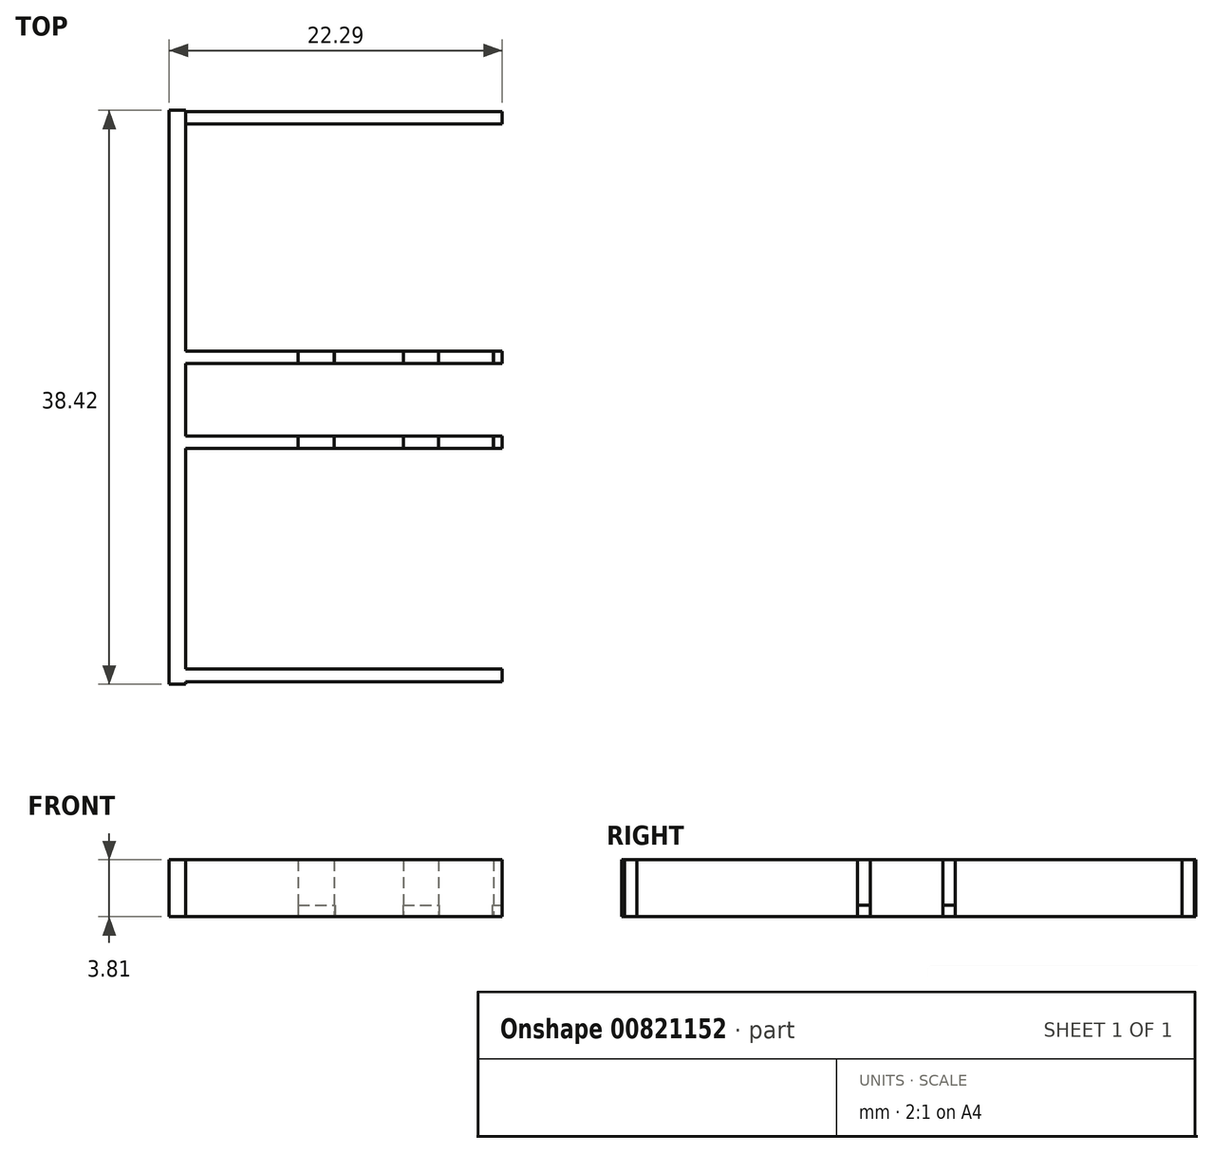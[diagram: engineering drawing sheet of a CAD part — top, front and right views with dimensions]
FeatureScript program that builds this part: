
annotation { "Feature Type Name" : "Feature", "Feature Type Description" : "" }
export const myFeature = defineFeature(function(context is Context, id is Id, definition is map)
    precondition{}
    {
        {
            var Q0;
            Q0=qCreatedBy(makeId("Top.planeOp"),FACE);
            var sketch = newSketch(context, id + "F0", { "sketchPlane" : qUnion([Q0])});
            skLineSegment(sketch, "E0.bottom", {"start": v(-54.97, 0.72) * mm, "end": v(-76.14, 0.72) * mm});
            skLineSegment(sketch, "E0.top", {"start": v(-54.97, -0.12) * mm, "end": v(-76.14, -0.12) * mm});
            skLineSegment(sketch, "E0.left", {"start": v(-54.97, 0.72) * mm, "end": v(-54.97, -0.12) * mm});
            skLineSegment(sketch, "E0.right", {"start": v(-76.14, 0.72) * mm, "end": v(-76.14, -0.12) * mm});
            skLineSegment(sketch, "E1.bottom", {"start": v(-66.2, -15.3) * mm, "end": v(-61.58, -15.3) * mm});
            skLineSegment(sketch, "E1.top", {"start": v(-66.2, -16.14) * mm, "end": v(-61.58, -16.14) * mm});
            skLineSegment(sketch, "E1.left", {"start": v(-66.2, -15.3) * mm, "end": v(-66.2, -16.14) * mm});
            skLineSegment(sketch, "E1.right", {"start": v(-61.58, -15.3) * mm, "end": v(-61.58, -16.14) * mm});
            skLineSegment(sketch, "E2.bottom", {"start": v(-66.2, -20.99) * mm, "end": v(-61.58, -20.99) * mm});
            skLineSegment(sketch, "E2.top", {"start": v(-66.2, -21.83) * mm, "end": v(-61.58, -21.83) * mm});
            skLineSegment(sketch, "E2.left", {"start": v(-66.2, -20.99) * mm, "end": v(-66.2, -21.83) * mm});
            skLineSegment(sketch, "E2.right", {"start": v(-61.58, -20.99) * mm, "end": v(-61.58, -21.83) * mm});
            skLineSegment(sketch, "E3.bottom", {"start": v(-59.25, -21.83) * mm, "end": v(-55.56, -21.83) * mm});
            skLineSegment(sketch, "E3.top", {"start": v(-59.25, -20.99) * mm, "end": v(-55.56, -20.99) * mm});
            skLineSegment(sketch, "E3.left", {"start": v(-59.25, -21.83) * mm, "end": v(-59.25, -20.99) * mm});
            skLineSegment(sketch, "E3.right", {"start": v(-55.56, -21.83) * mm, "end": v(-55.56, -20.99) * mm});
            skLineSegment(sketch, "E4.bottom", {"start": v(-59.25, -15.3) * mm, "end": v(-55.56, -15.3) * mm});
            skLineSegment(sketch, "E4.top", {"start": v(-59.25, -16.14) * mm, "end": v(-55.56, -16.14) * mm});
            skLineSegment(sketch, "E4.left", {"start": v(-59.25, -15.3) * mm, "end": v(-59.25, -16.14) * mm});
            skLineSegment(sketch, "E4.right", {"start": v(-55.56, -15.3) * mm, "end": v(-55.56, -16.14) * mm});
            skLineSegment(sketch, "E5.bottom", {"start": v(-77.25, -15.3) * mm, "end": v(-68.62, -15.3) * mm});
            skLineSegment(sketch, "E5.top", {"start": v(-77.25, -16.14) * mm, "end": v(-68.62, -16.14) * mm});
            skLineSegment(sketch, "E5.left", {"start": v(-77.25, -15.3) * mm, "end": v(-77.25, -16.14) * mm});
            skLineSegment(sketch, "E5.right", {"start": v(-68.62, -15.3) * mm, "end": v(-68.62, -16.14) * mm});
            skLineSegment(sketch, "E6.bottom", {"start": v(-77.25, -20.99) * mm, "end": v(-68.62, -20.99) * mm});
            skLineSegment(sketch, "E6.top", {"start": v(-77.25, -21.83) * mm, "end": v(-68.62, -21.83) * mm});
            skLineSegment(sketch, "E6.left", {"start": v(-77.25, -20.99) * mm, "end": v(-77.25, -21.83) * mm});
            skLineSegment(sketch, "E6.right", {"start": v(-68.62, -20.99) * mm, "end": v(-68.62, -21.83) * mm});
            skLineSegment(sketch, "E7.bottom", {"start": v(-77.2, -36.6) * mm, "end": v(-54.97, -36.6) * mm});
            skLineSegment(sketch, "E7.top", {"start": v(-77.2, -37.43) * mm, "end": v(-54.97, -37.43) * mm});
            skLineSegment(sketch, "E7.left", {"start": v(-77.2, -36.6) * mm, "end": v(-77.2, -37.43) * mm});
            skLineSegment(sketch, "E7.right", {"start": v(-54.97, -36.6) * mm, "end": v(-54.97, -37.43) * mm});
            skLineSegment(sketch, "E8.left", {"start": v(-77.26, 0.8) * mm, "end": v(-77.26, -37.6) * mm});
            skLineSegment(sketch, "E8.right", {"start": v(-76.15, 0.8) * mm, "end": v(-76.15, -37.6) * mm});
            skLineSegment(sketch, "E9", {"start": v(-54.97, -37.6) * mm, "end": v(-54.97, 0.8) * mm});
            skLineSegment(sketch, "E10", {"start": v(-77.26, -37.6) * mm, "end": v(-76.15, -37.6) * mm});
            skLineSegment(sketch, "E11", {"start": v(-77.26, 0.8) * mm, "end": v(-76.15, 0.8) * mm});
            skSolve(sketch);
        }
        {
            var Q0;
            Q0 = qSketchRegion(id + "F0", true);
            extrude(context, id + "F1", {"entities" : qUnion([Q0]), "depth" : 3.8 * mm, "offsetDistance" : 25.4 * mm});
        }
        {
            var Q0;
            Q0=qCreatedBy(makeId("Top.planeOp"),FACE);
            var sketch = newSketch(context, id + "F2", { "sketchPlane" : qUnion([Q0])});
            skLineSegment(sketch, "E12.bottom", {"start": v(-68.62, -15.3) * mm, "end": v(-66.16, -15.3) * mm});
            skLineSegment(sketch, "E12.top", {"start": v(-68.62, -16.14) * mm, "end": v(-66.16, -16.14) * mm});
            skLineSegment(sketch, "E12.left", {"start": v(-68.62, -15.3) * mm, "end": v(-68.62, -16.14) * mm});
            skLineSegment(sketch, "E12.right", {"start": v(-66.16, -15.3) * mm, "end": v(-66.16, -16.14) * mm});
            skLineSegment(sketch, "E13.bottom", {"start": v(-68.64, -20.99) * mm, "end": v(-66.18, -20.99) * mm});
            skLineSegment(sketch, "E13.top", {"start": v(-68.64, -21.83) * mm, "end": v(-66.18, -21.83) * mm});
            skLineSegment(sketch, "E13.left", {"start": v(-68.64, -20.99) * mm, "end": v(-68.64, -21.83) * mm});
            skLineSegment(sketch, "E13.right", {"start": v(-66.18, -20.99) * mm, "end": v(-66.18, -21.83) * mm});
            skLineSegment(sketch, "E14.bottom", {"start": v(-61.62, -15.3) * mm, "end": v(-59.2, -15.3) * mm});
            skLineSegment(sketch, "E14.top", {"start": v(-61.62, -16.14) * mm, "end": v(-59.2, -16.14) * mm});
            skLineSegment(sketch, "E14.left", {"start": v(-61.62, -15.3) * mm, "end": v(-61.62, -16.14) * mm});
            skLineSegment(sketch, "E14.right", {"start": v(-59.2, -15.3) * mm, "end": v(-59.2, -16.14) * mm});
            skLineSegment(sketch, "E15.bottom", {"start": v(-61.6, -20.99) * mm, "end": v(-59.19, -20.99) * mm});
            skLineSegment(sketch, "E15.top", {"start": v(-61.6, -21.83) * mm, "end": v(-59.19, -21.83) * mm});
            skLineSegment(sketch, "E15.left", {"start": v(-61.6, -20.99) * mm, "end": v(-61.6, -21.83) * mm});
            skLineSegment(sketch, "E15.right", {"start": v(-59.19, -20.99) * mm, "end": v(-59.19, -21.83) * mm});
            skLineSegment(sketch, "E16.bottom", {"start": v(-55.64, -15.3) * mm, "end": v(-54.97, -15.3) * mm});
            skLineSegment(sketch, "E16.top", {"start": v(-55.64, -16.14) * mm, "end": v(-54.97, -16.14) * mm});
            skLineSegment(sketch, "E16.left", {"start": v(-55.64, -15.3) * mm, "end": v(-55.64, -16.14) * mm});
            skLineSegment(sketch, "E16.right", {"start": v(-54.97, -15.3) * mm, "end": v(-54.97, -16.14) * mm});
            skLineSegment(sketch, "E17.bottom", {"start": v(-55.64, -20.99) * mm, "end": v(-54.97, -20.99) * mm});
            skLineSegment(sketch, "E17.top", {"start": v(-55.64, -21.83) * mm, "end": v(-54.97, -21.83) * mm});
            skLineSegment(sketch, "E17.left", {"start": v(-55.64, -20.99) * mm, "end": v(-55.64, -21.83) * mm});
            skLineSegment(sketch, "E17.right", {"start": v(-54.97, -20.99) * mm, "end": v(-54.97, -21.83) * mm});
            skSolve(sketch);
        }
        {
            var Q0;
            Q0 = qSketchRegion(id + "F2", true);
            extrude(context, id + "F3", {"entities" : qUnion([Q0]), "depth" : 0.76 * mm, "offsetDistance" : 25.4 * mm});
        }
    });
